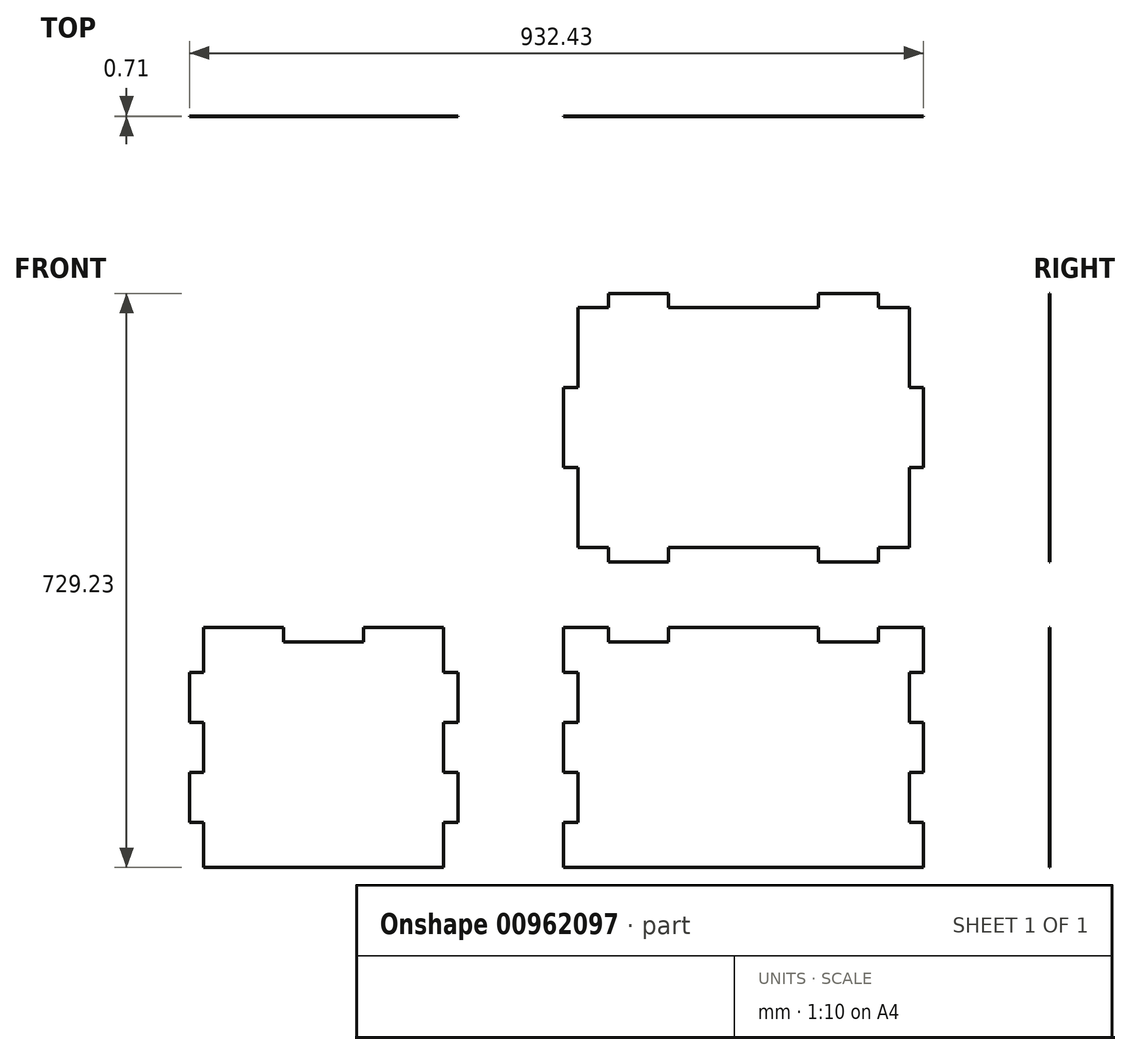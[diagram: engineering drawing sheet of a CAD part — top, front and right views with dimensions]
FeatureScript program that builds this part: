
annotation { "Feature Type Name" : "Feature", "Feature Type Description" : "" }
export const myFeature = defineFeature(function(context is Context, id is Id, definition is map)
    precondition{}
    {
        {
            assignVariable(context, id + "F0", {"name" : "ply34", "anyValue" : .71});
        }
        {
            var Q0;
            Q0=qCreatedBy(makeId("Front.planeOp"),FACE);
            var sketch = newSketch(context, id + "F1", { "sketchPlane" : qUnion([Q0])});
            skLineSegment(sketch, "E0.bottom", {"start": v(-228.6, 152.4) * mm, "end": v(228.6, 152.4) * mm});
            skLineSegment(sketch, "E0.top", {"start": v(-228.6, -152.4) * mm, "end": v(228.6, -152.4) * mm});
            skLineSegment(sketch, "E0.left", {"start": v(-228.6, 152.4) * mm, "end": v(-228.6, -152.4) * mm});
            skLineSegment(sketch, "E0.right", {"start": v(228.6, 152.4) * mm, "end": v(228.6, -152.4) * mm});
            skPoint(sketch, "E0.middle", {"position": v(0, 0) * mm});
            skLineSegment(sketch, "E1.bottom", {"start": v(-381, 152.4) * mm, "end": v(-685.8, 152.4) * mm});
            skLineSegment(sketch, "E1.top", {"start": v(-381, -152.4) * mm, "end": v(-685.8, -152.4) * mm});
            skLineSegment(sketch, "E1.left", {"start": v(-381, 152.4) * mm, "end": v(-381, -152.4) * mm});
            skLineSegment(sketch, "E1.right", {"start": v(-685.8, 152.4) * mm, "end": v(-685.8, -152.4) * mm});
            skLineSegment(sketch, "E2.bottom", {"start": v(-381, 95.25) * mm, "end": v(-362.97, 95.25) * mm});
            skLineSegment(sketch, "E2.top", {"start": v(-381, 31.75) * mm, "end": v(-362.97, 31.75) * mm});
            skLineSegment(sketch, "E2.left", {"start": v(-381, 95.25) * mm, "end": v(-381, 31.75) * mm});
            skLineSegment(sketch, "E2.right", {"start": v(-362.97, 95.25) * mm, "end": v(-362.97, 31.75) * mm});
            skLineSegment(sketch, "E3", {"start": v(-228.6, 0) * mm, "end": v(-381, 0) * mm, "construction": true});
            skLineSegment(sketch, "E4.MirrorCS", {"start": v(-381, -95.25) * mm, "end": v(-362.97, -95.25) * mm});
            skLineSegment(sketch, "E5.MirrorCS", {"start": v(-381, -31.75) * mm, "end": v(-362.97, -31.75) * mm});
            skLineSegment(sketch, "E6.MirrorCS", {"start": v(-381, -95.25) * mm, "end": v(-381, -31.75) * mm});
            skLineSegment(sketch, "E7.MirrorCS", {"start": v(-362.97, -95.25) * mm, "end": v(-362.97, -31.75) * mm});
            skLineSegment(sketch, "E8", {"start": v(-362.97, 63.5) * mm, "end": v(-228.6, 63.5) * mm, "construction": true});
            skLineSegment(sketch, "E9", {"start": v(-295.78, 63.5) * mm, "end": v(-295.78, 0) * mm, "construction": true});
            skLineSegment(sketch, "E10.MirrorCS", {"start": v(-210.57, 95.25) * mm, "end": v(-228.6, 95.25) * mm});
            skLineSegment(sketch, "E11.MirrorCS", {"start": v(-210.57, -95.25) * mm, "end": v(-228.6, -95.25) * mm});
            skLineSegment(sketch, "E12.MirrorCS", {"start": v(-210.57, 31.75) * mm, "end": v(-228.6, 31.75) * mm});
            skLineSegment(sketch, "E13.MirrorCS", {"start": v(-210.57, -31.75) * mm, "end": v(-228.6, -31.75) * mm});
            skLineSegment(sketch, "E14.MirrorCS", {"start": v(-210.57, 95.25) * mm, "end": v(-210.57, 31.75) * mm});
            skLineSegment(sketch, "E15.MirrorCS", {"start": v(-228.6, -95.25) * mm, "end": v(-228.6, -31.75) * mm});
            skLineSegment(sketch, "E16.MirrorCS", {"start": v(-228.6, 95.25) * mm, "end": v(-228.6, 31.75) * mm});
            skLineSegment(sketch, "E17.MirrorCS", {"start": v(-210.57, -95.25) * mm, "end": v(-210.57, -31.75) * mm});
            skLineSegment(sketch, "E18", {"start": v(-533.4, 152.4) * mm, "end": v(-533.4, -152.4) * mm, "construction": true});
            skLineSegment(sketch, "E19", {"start": v(0, 152.4) * mm, "end": v(0, -152.4) * mm, "construction": true});
            skLineSegment(sketch, "E20.MirrorCS", {"start": v(-703.83, 95.25) * mm, "end": v(-703.83, 31.75) * mm});
            skLineSegment(sketch, "E21.MirrorCS", {"start": v(-685.8, 31.75) * mm, "end": v(-703.83, 31.75) * mm});
            skLineSegment(sketch, "E22.MirrorCS", {"start": v(-685.8, -95.25) * mm, "end": v(-703.83, -95.25) * mm});
            skLineSegment(sketch, "E23.MirrorCS", {"start": v(-685.8, -31.75) * mm, "end": v(-703.83, -31.75) * mm});
            skLineSegment(sketch, "E24.MirrorCS", {"start": v(-685.8, 95.25) * mm, "end": v(-703.83, 95.25) * mm});
            skLineSegment(sketch, "E25.MirrorCS", {"start": v(-685.8, 95.25) * mm, "end": v(-685.8, 31.75) * mm});
            skLineSegment(sketch, "E26.MirrorCS", {"start": v(-703.83, -95.25) * mm, "end": v(-703.83, -31.75) * mm});
            skLineSegment(sketch, "E27.MirrorCS", {"start": v(-685.8, -95.25) * mm, "end": v(-685.8, -31.75) * mm});
            skLineSegment(sketch, "E28.MirrorCS", {"start": v(210.57, -31.75) * mm, "end": v(228.6, -31.75) * mm});
            skLineSegment(sketch, "E29.MirrorCS", {"start": v(210.57, -95.25) * mm, "end": v(228.6, -95.25) * mm});
            skLineSegment(sketch, "E30.MirrorCS", {"start": v(210.57, 31.75) * mm, "end": v(228.6, 31.75) * mm});
            skLineSegment(sketch, "E31.MirrorCS", {"start": v(210.57, 95.25) * mm, "end": v(228.6, 95.25) * mm});
            skLineSegment(sketch, "E32.MirrorCS", {"start": v(228.6, 95.25) * mm, "end": v(228.6, 31.75) * mm});
            skLineSegment(sketch, "E33.MirrorCS", {"start": v(228.6, -95.25) * mm, "end": v(228.6, -31.75) * mm});
            skLineSegment(sketch, "E34.MirrorCS", {"start": v(210.57, -95.25) * mm, "end": v(210.57, -31.75) * mm});
            skLineSegment(sketch, "E35.MirrorCS", {"start": v(210.57, 95.25) * mm, "end": v(210.57, 31.75) * mm});
            skLineSegment(sketch, "E36.bottom", {"start": v(-171.45, 152.4) * mm, "end": v(-95.25, 152.4) * mm});
            skLineSegment(sketch, "E36.top", {"start": v(-171.45, 134.37) * mm, "end": v(-95.25, 134.37) * mm});
            skLineSegment(sketch, "E36.left", {"start": v(-171.45, 152.4) * mm, "end": v(-171.45, 134.37) * mm});
            skLineSegment(sketch, "E36.right", {"start": v(-95.25, 152.4) * mm, "end": v(-95.25, 134.37) * mm});
            skLineSegment(sketch, "E37.MirrorCS", {"start": v(171.45, 152.4) * mm, "end": v(171.45, 134.37) * mm});
            skLineSegment(sketch, "E38.MirrorCS", {"start": v(171.45, 152.4) * mm, "end": v(95.25, 152.4) * mm});
            skLineSegment(sketch, "E39.MirrorCS", {"start": v(171.45, 134.37) * mm, "end": v(95.25, 134.37) * mm});
            skLineSegment(sketch, "E40.MirrorCS", {"start": v(95.25, 152.4) * mm, "end": v(95.25, 134.37) * mm});
            skLineSegment(sketch, "E41.bottom", {"start": v(-171.45, 254) * mm, "end": v(-95.25, 254) * mm});
            skLineSegment(sketch, "E41.top", {"start": v(-171.45, 235.97) * mm, "end": v(-95.25, 235.97) * mm});
            skLineSegment(sketch, "E41.left", {"start": v(-171.45, 254) * mm, "end": v(-171.45, 235.97) * mm});
            skLineSegment(sketch, "E41.right", {"start": v(-95.25, 254) * mm, "end": v(-95.25, 235.97) * mm});
            skLineSegment(sketch, "E42.MirrorCS", {"start": v(95.25, 254) * mm, "end": v(95.25, 235.97) * mm});
            skLineSegment(sketch, "E43.MirrorCS", {"start": v(171.45, 235.97) * mm, "end": v(95.25, 235.97) * mm});
            skLineSegment(sketch, "E44.MirrorCS", {"start": v(171.45, 254) * mm, "end": v(95.25, 254) * mm});
            skLineSegment(sketch, "E45.MirrorCS", {"start": v(171.45, 254) * mm, "end": v(171.45, 235.97) * mm});
            skLineSegment(sketch, "E46", {"start": v(-210.57, 406.4) * mm, "end": v(210.57, 406.4) * mm, "construction": true});
            skLineSegment(sketch, "E47.MirrorCS", {"start": v(-95.25, 558.8) * mm, "end": v(-95.25, 576.83) * mm});
            skLineSegment(sketch, "E48.MirrorCS", {"start": v(95.25, 558.8) * mm, "end": v(95.25, 576.83) * mm});
            skLineSegment(sketch, "E49.MirrorCS", {"start": v(171.45, 558.8) * mm, "end": v(95.25, 558.8) * mm});
            skLineSegment(sketch, "E50.MirrorCS", {"start": v(-171.45, 576.83) * mm, "end": v(-95.25, 576.83) * mm});
            skLineSegment(sketch, "E51.MirrorCS", {"start": v(-171.45, 558.8) * mm, "end": v(-95.25, 558.8) * mm});
            skLineSegment(sketch, "E52.MirrorCS", {"start": v(171.45, 558.8) * mm, "end": v(171.45, 576.83) * mm});
            skLineSegment(sketch, "E53.MirrorCS", {"start": v(171.45, 576.83) * mm, "end": v(95.25, 576.83) * mm});
            skLineSegment(sketch, "E54.MirrorCS", {"start": v(-171.45, 558.8) * mm, "end": v(-171.45, 576.83) * mm});
            skLineSegment(sketch, "E55.bottom", {"start": v(-210.57, 254) * mm, "end": v(210.57, 254) * mm});
            skLineSegment(sketch, "E55.top", {"start": v(-210.57, 558.8) * mm, "end": v(210.57, 558.8) * mm});
            skLineSegment(sketch, "E55.left", {"start": v(-210.57, 254) * mm, "end": v(-210.57, 558.8) * mm});
            skLineSegment(sketch, "E55.right", {"start": v(210.57, 254) * mm, "end": v(210.57, 558.8) * mm});
            skLineSegment(sketch, "E56.bottom", {"start": v(-210.57, 457.2) * mm, "end": v(-192.53, 457.2) * mm, "construction": true});
            skLineSegment(sketch, "E56.top", {"start": v(-210.57, 355.6) * mm, "end": v(-192.53, 355.6) * mm, "construction": true});
            skLineSegment(sketch, "E56.left", {"start": v(-210.57, 457.2) * mm, "end": v(-210.57, 355.6) * mm});
            skLineSegment(sketch, "E56.right", {"start": v(-192.53, 457.2) * mm, "end": v(-192.53, 355.6) * mm, "construction": true});
            skPoint(sketch, "E56.middle", {"position": v(-201.55, 406.4) * mm});
            skLineSegment(sketch, "E57.MirrorCS", {"start": v(210.57, 355.6) * mm, "end": v(192.53, 355.6) * mm, "construction": true});
            skLineSegment(sketch, "E58.MirrorCS", {"start": v(210.57, 457.2) * mm, "end": v(192.53, 457.2) * mm, "construction": true});
            skLineSegment(sketch, "E59.MirrorCS", {"start": v(210.57, 457.2) * mm, "end": v(210.57, 355.6) * mm});
            skPoint(sketch, "E60.MirrorP", {"position": v(201.55, 406.4) * mm});
            skLineSegment(sketch, "E61.MirrorCS", {"start": v(192.53, 457.2) * mm, "end": v(192.53, 355.6) * mm, "construction": true});
            skLineSegment(sketch, "E62.MirrorCS", {"start": v(-210.57, 355.6) * mm, "end": v(-228.6, 355.6) * mm});
            skLineSegment(sketch, "E63.MirrorCS", {"start": v(-228.6, 457.2) * mm, "end": v(-228.6, 355.6) * mm});
            skLineSegment(sketch, "E64.MirrorCS", {"start": v(-210.57, 457.2) * mm, "end": v(-228.6, 457.2) * mm});
            skLineSegment(sketch, "E65.MirrorCS", {"start": v(210.57, 355.6) * mm, "end": v(228.6, 355.6) * mm});
            skLineSegment(sketch, "E66.MirrorCS", {"start": v(228.6, 457.2) * mm, "end": v(228.6, 355.6) * mm});
            skLineSegment(sketch, "E67.MirrorCS", {"start": v(210.57, 457.2) * mm, "end": v(228.6, 457.2) * mm});
            skLineSegment(sketch, "E68.bottom", {"start": v(-584.2, 152.4) * mm, "end": v(-482.6, 152.4) * mm});
            skLineSegment(sketch, "E68.top", {"start": v(-584.2, 134.37) * mm, "end": v(-482.6, 134.37) * mm});
            skLineSegment(sketch, "E68.left", {"start": v(-584.2, 152.4) * mm, "end": v(-584.2, 134.37) * mm});
            skLineSegment(sketch, "E68.right", {"start": v(-482.6, 152.4) * mm, "end": v(-482.6, 134.37) * mm});
            skPoint(sketch, "E68.middle", {"position": v(-533.4, 143.38) * mm});
            skSolve(sketch);
        }
        {
            var Q0;
            {var subQ6=sQuery(id+"F1.wireOp",EDGE,"E1.top");Q0=makeQuery(id+"F1.imprint","IMPRINT",FACE,{"disambiguationData":[TD([[makeQuery(id+"F1.imprint","IMPRINT",EDGE,{"derivedFrom":subQ6}),-1.0]])]});}
            var Q1;
            Q1=makeQuery(id+"F1.imprint","IMPRINT",FACE,{"disambiguationData":[TD([[makeQuery(id+"F1.imprint","IMPRINT",EDGE,{"derivedFrom":sQuery(id+"F1.wireOp",EDGE,"E20.MirrorCS")}),1.0]])]});
            var Q2;
            {var subQ0=sQuery(id+"F1.wireOp",EDGE,"E22.MirrorCS");Q2=makeQuery(id+"F1.imprint","IMPRINT",FACE,{"disambiguationData":[TD([[makeQuery(id+"F1.imprint","IMPRINT",EDGE,{"derivedFrom":subQ0}),-1.0]])]});}
            var Q3;
            {var subQ2=sQuery(id+"F1.wireOp",EDGE,"E2.bottom");Q3=makeQuery(id+"F1.imprint","IMPRINT",FACE,{"disambiguationData":[TD([[makeQuery(id+"F1.imprint","IMPRINT",EDGE,{"derivedFrom":subQ2}),-1.0]])]});}
            var Q4;
            {var subQ0=sQuery(id+"F1.wireOp",EDGE,"E4.MirrorCS");Q4=makeQuery(id+"F1.imprint","IMPRINT",FACE,{"disambiguationData":[TD([[makeQuery(id+"F1.imprint","IMPRINT",EDGE,{"derivedFrom":subQ0}),1.0]])]});}
            var Q5;
            {var subQ0=sQuery(id+"F1.wireOp",EDGE,"E0.top");Q5=makeQuery(id+"F1.imprint","IMPRINT",FACE,{"disambiguationData":[TD([[makeQuery(id+"F1.imprint","IMPRINT",EDGE,{"derivedFrom":subQ0}),1.0]])]});}
            var Q6;
            {var subQ18=sQuery(id+"F1.wireOp",EDGE,"E56.bottom");Q6=makeQuery(id+"F1.imprint","IMPRINT",FACE,{"disambiguationData":[TD([[makeQuery(id+"F1.imprint","IMPRINT",EDGE,{"derivedFrom":subQ18}),1.0]])]});}
            var Q7;
            Q7=makeQuery(id+"F1.imprint","IMPRINT",FACE,{"disambiguationData":[TD([[makeQuery(id+"F1.imprint","IMPRINT",EDGE,{"derivedFrom":sQuery(id+"F1.wireOp",EDGE,"E47.MirrorCS")}),1.0]])]});
            var Q8;
            Q8=makeQuery(id+"F1.imprint","IMPRINT",FACE,{"disambiguationData":[TD([[makeQuery(id+"F1.imprint","IMPRINT",EDGE,{"derivedFrom":sQuery(id+"F1.wireOp",EDGE,"E48.MirrorCS")}),-1.0]])]});
            var Q9;
            Q9=makeQuery(id+"F1.imprint","IMPRINT",FACE,{"disambiguationData":[TD([[makeQuery(id+"F1.imprint","IMPRINT",EDGE,{"derivedFrom":sQuery(id+"F1.wireOp",EDGE,"E42.MirrorCS")}),1.0]])]});
            var Q10;
            Q10=makeQuery(id+"F1.imprint","IMPRINT",FACE,{"disambiguationData":[TD([[makeQuery(id+"F1.imprint","IMPRINT",EDGE,{"derivedFrom":sQuery(id+"F1.wireOp",EDGE,"E41.bottom")}),-1.0]])]});
            var Q11;
            {var subQ6=sQuery(id+"F1.wireOp",EDGE,"E41.bottom");Q11=makeQuery(id+"F1.imprint","IMPRINT",FACE,{"disambiguationData":[TD([[makeQuery(id+"F1.imprint","IMPRINT",EDGE,{"derivedFrom":subQ6}),1.0]])]});}
            var Q12;
            {var subQ0=sQuery(id+"F1.wireOp",EDGE,"E62.MirrorCS");Q12=makeQuery(id+"F1.imprint","IMPRINT",FACE,{"disambiguationData":[TD([[makeQuery(id+"F1.imprint","IMPRINT",EDGE,{"derivedFrom":subQ0}),-1.0]])]});}
            var Q13;
            {var subQ0=sQuery(id+"F1.wireOp",EDGE,"E65.MirrorCS");Q13=makeQuery(id+"F1.imprint","IMPRINT",FACE,{"disambiguationData":[TD([[makeQuery(id+"F1.imprint","IMPRINT",EDGE,{"derivedFrom":subQ0}),1.0]])]});}
            extrude(context, id + "F2", {"entities" : qUnion([Q0, Q1, Q2, Q3, Q4, Q5, Q6, Q7, Q8, Q9, Q10, Q11, Q12, Q13]), "depth" : (getVariable(context, 'ply34')) * mm, "offsetDistance" : 25.4 * mm});
        }
    });
